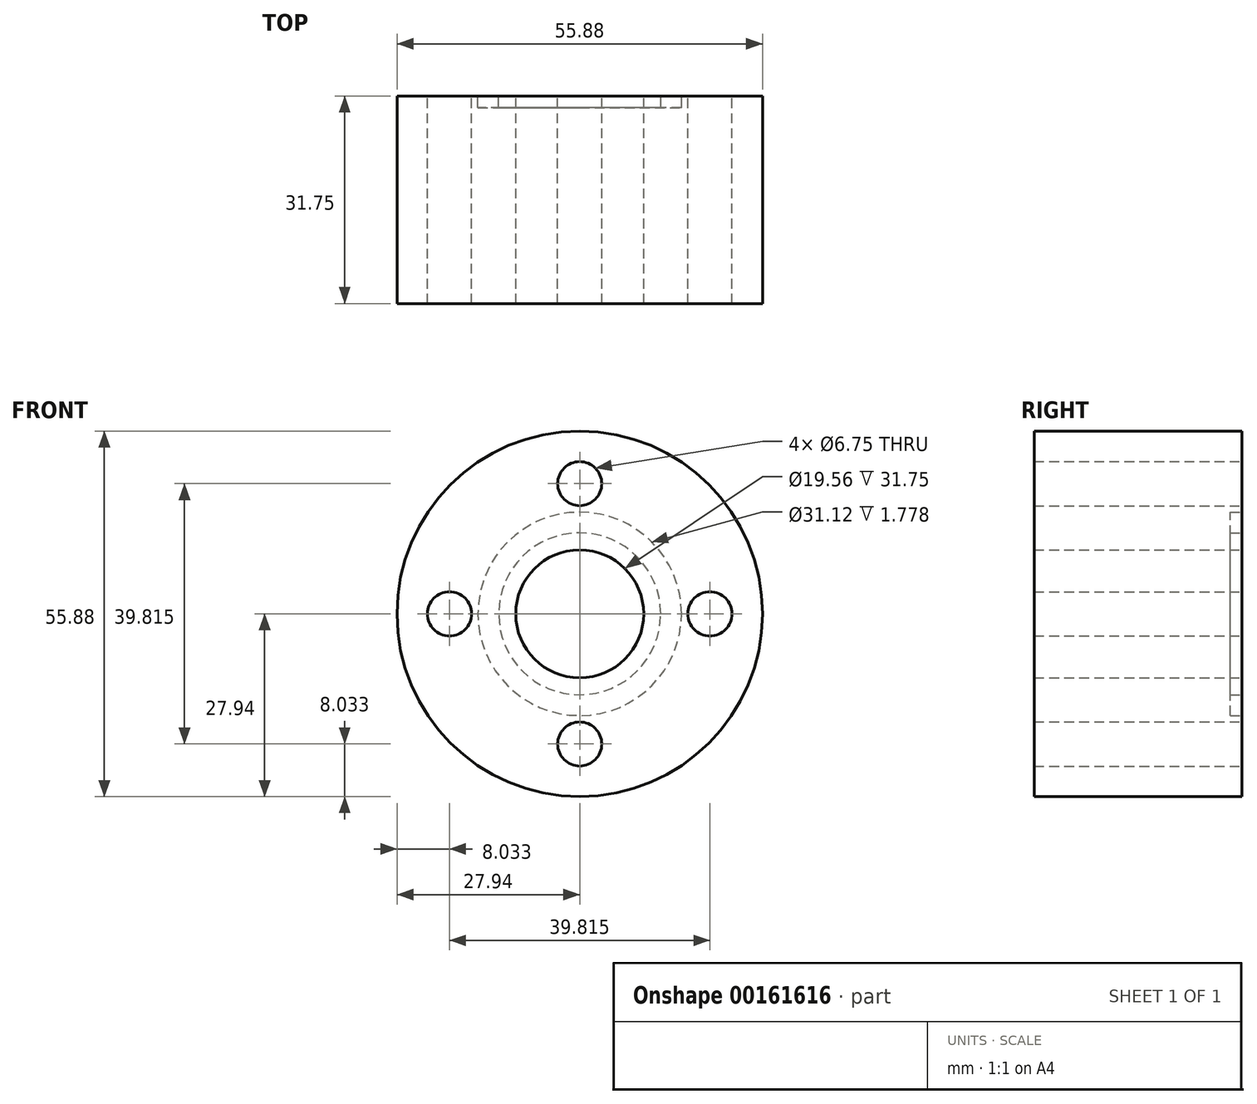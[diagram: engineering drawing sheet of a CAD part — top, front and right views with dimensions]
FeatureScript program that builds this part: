
annotation { "Feature Type Name" : "Feature", "Feature Type Description" : "" }
export const myFeature = defineFeature(function(context is Context, id is Id, definition is map)
    precondition{}
    {
        {
            var Q0;
            Q0=qCreatedBy(makeId("Front.planeOp"),FACE);
            var sketch = newSketch(context, id + "F0", { "sketchPlane" : qUnion([Q0])});
            skCircle(sketch, "E0", {"center": v(0, 0) * mm, "radius": 27.94 * mm});
            skCircle(sketch, "E1", {"center": v(0, 0) * mm, "radius": 9.78 * mm});
            skCircle(sketch, "E2", {"center": v(-19.9, 0) * mm, "radius": 3.37 * mm});
            skCircle(sketch, "E3.1.0", {"center": v(0, -19.9) * mm, "radius": 3.37 * mm});
            skCircle(sketch, "E3.2.0", {"center": v(19.9, 0) * mm, "radius": 3.37 * mm});
            skCircle(sketch, "E3.3.0", {"center": v(0, 19.9) * mm, "radius": 3.37 * mm});
            skSolve(sketch);
        }
        {
            var Q0;
            Q0=makeQuery(id+"F0.imprint","IMPRINT",FACE,{"disambiguationData":[TD([[makeQuery(id+"F0.imprint","IMPRINT",EDGE,{"derivedFrom":sQuery(id+"F0.wireOp",EDGE,"E0")}),1.0]])]});
            extrude(context, id + "F1", {"entities" : qUnion([Q0]), "depth" : 31.75 * mm});
        }
        {
            var Q0;
            Q0=qCreatedBy(makeId("Front.planeOp"),FACE);
            var sketch = newSketch(context, id + "F2", { "sketchPlane" : qUnion([Q0])});
            skCircle(sketch, "E4", {"center": v(0, 0) * mm, "radius": 15.56 * mm});
            skCircle(sketch, "E5.0", {"center": v(0, 0) * mm, "radius": 12.38 * mm});
            skSolve(sketch);
        }
        {
            var Q0;
            Q0=makeQuery(id+"F2.imprint","IMPRINT",FACE,{"disambiguationData":[TD([[makeQuery(id+"F2.imprint","IMPRINT",EDGE,{"derivedFrom":sQuery(id+"F2.wireOp",EDGE,"E4")}),1.0]])]});
            extrude(context, id + "F3", {"entities" : qUnion([Q0]), "operationType" : NewBodyOperationType.REMOVE, "depth" : 1.78 * mm});
        }
    });
